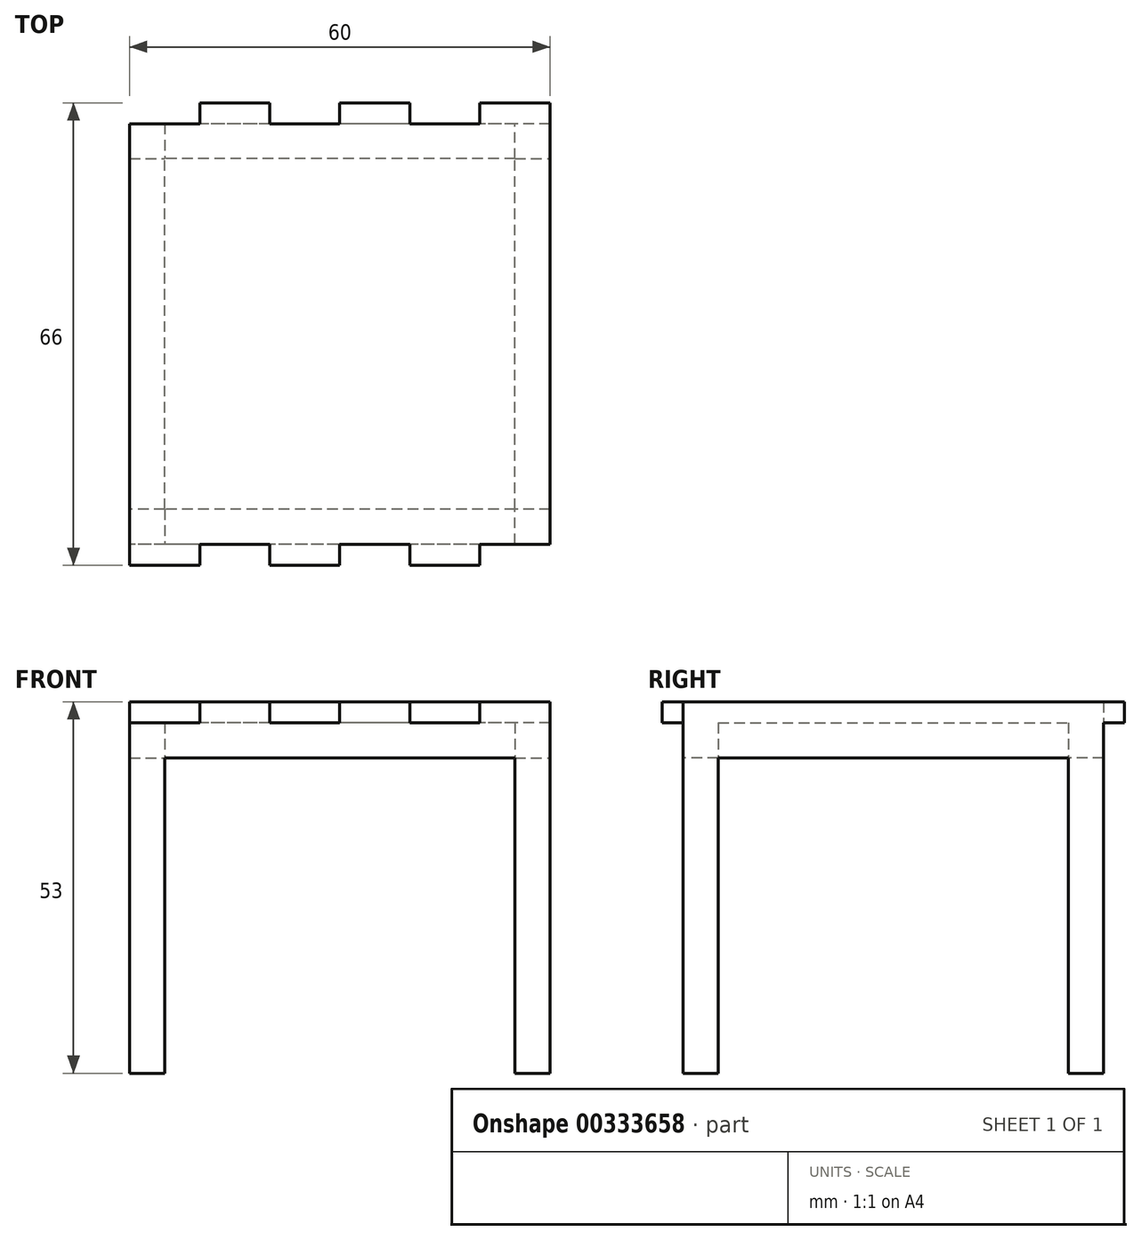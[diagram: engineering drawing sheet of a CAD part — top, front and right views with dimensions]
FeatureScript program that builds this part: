
annotation { "Feature Type Name" : "Feature", "Feature Type Description" : "" }
export const myFeature = defineFeature(function(context is Context, id is Id, definition is map)
    precondition{}
    {
        {
            var Q0;
            Q0=qCreatedBy(makeId("Top.planeOp"),FACE);
            var sketch = newSketch(context, id + "F0", { "sketchPlane" : qUnion([Q0])});
            skLineSegment(sketch, "E0.bottom", {"start": v(0, 0) * mm, "end": v(-60, 0) * mm});
            skLineSegment(sketch, "E0.top", {"start": v(0, 60) * mm, "end": v(-60, 60) * mm});
            skLineSegment(sketch, "E0.left", {"start": v(0, 0) * mm, "end": v(0, 60) * mm});
            skLineSegment(sketch, "E0.right", {"start": v(-60, 0) * mm, "end": v(-60, 60) * mm});
            skLineSegment(sketch, "E1.0", {"start": v(-5, 5) * mm, "end": v(-55, 5) * mm});
            skLineSegment(sketch, "E1.1", {"start": v(-5, 5) * mm, "end": v(-5, 55) * mm});
            skLineSegment(sketch, "E1.2", {"start": v(-5, 55) * mm, "end": v(-55, 55) * mm});
            skLineSegment(sketch, "E1.3", {"start": v(-55, 5) * mm, "end": v(-55, 55) * mm});
            skSolve(sketch);
        }
        {
            var Q0;
            Q0 = qSketchRegion(id + "F0", true);
            extrude(context, id + "F1", {"entities" : qUnion([Q0]), "depth" : 5 * mm});
        }
        {
            var Q0;
            Q0=makeQuery(id+"F1.opExtrude","CAP_FACE",FACE,{"disambiguationData":[OSD([sQuery(id+"F0.wireOp",EDGE,"E0.bottom"),sQuery(id+"F0.wireOp",EDGE,"E0.top"),sQuery(id+"F0.wireOp",EDGE,"E0.left"),sQuery(id+"F0.wireOp",EDGE,"E0.right"),sQuery(id+"F0.wireOp",EDGE,"E1.0"),sQuery(id+"F0.wireOp",EDGE,"E1.1"),sQuery(id+"F0.wireOp",EDGE,"E1.2"),sQuery(id+"F0.wireOp",EDGE,"E1.3")])],"isStart":true});
            var sketch = newSketch(context, id + "F2", { "sketchPlane" : qUnion([Q0])});
            skLineSegment(sketch, "E2.bottom", {"start": v(0, 0) * mm, "end": v(-5, 0) * mm});
            skLineSegment(sketch, "E2.top", {"start": v(0, -5) * mm, "end": v(-5, -5) * mm});
            skLineSegment(sketch, "E2.left", {"start": v(0, 0) * mm, "end": v(0, -5) * mm});
            skLineSegment(sketch, "E2.right", {"start": v(-5, 0) * mm, "end": v(-5, -5) * mm});
            skLineSegment(sketch, "E3.bottom", {"start": v(-55, -5) * mm, "end": v(-60, -5) * mm});
            skLineSegment(sketch, "E3.top", {"start": v(-55, 0) * mm, "end": v(-60, 0) * mm});
            skLineSegment(sketch, "E3.left", {"start": v(-55, -5) * mm, "end": v(-55, 0) * mm});
            skLineSegment(sketch, "E3.right", {"start": v(-60, -5) * mm, "end": v(-60, 0) * mm});
            skLineSegment(sketch, "E4.bottom", {"start": v(-5, -55) * mm, "end": v(0, -55) * mm});
            skLineSegment(sketch, "E4.top", {"start": v(-5, -60) * mm, "end": v(0, -60) * mm});
            skLineSegment(sketch, "E4.left", {"start": v(-5, -55) * mm, "end": v(-5, -60) * mm});
            skLineSegment(sketch, "E4.right", {"start": v(0, -55) * mm, "end": v(0, -60) * mm});
            skLineSegment(sketch, "E5.bottom", {"start": v(-60, -60) * mm, "end": v(-55, -60) * mm});
            skLineSegment(sketch, "E5.top", {"start": v(-60, -55) * mm, "end": v(-55, -55) * mm});
            skLineSegment(sketch, "E5.left", {"start": v(-60, -60) * mm, "end": v(-60, -55) * mm});
            skLineSegment(sketch, "E5.right", {"start": v(-55, -60) * mm, "end": v(-55, -55) * mm});
            skSolve(sketch);
        }
        {
            var Q0;
            Q0 = qSketchRegion(id + "F2", true);
            extrude(context, id + "F3", {"entities" : qUnion([Q0]), "operationType" : NewBodyOperationType.ADD, "depth" : 45 * mm});
        }
        {
            var Q0;
            Q0=makeQuery(id+"F1.opExtrude","CAP_FACE",FACE,{"disambiguationData":[OSD([sQuery(id+"F0.wireOp",EDGE,"E0.bottom"),sQuery(id+"F0.wireOp",EDGE,"E0.top"),sQuery(id+"F0.wireOp",EDGE,"E0.left"),sQuery(id+"F0.wireOp",EDGE,"E0.right"),sQuery(id+"F0.wireOp",EDGE,"E1.0"),sQuery(id+"F0.wireOp",EDGE,"E1.1"),sQuery(id+"F0.wireOp",EDGE,"E1.2"),sQuery(id+"F0.wireOp",EDGE,"E1.3")])],"isStart":false});
            var sketch = newSketch(context, id + "F4", { "sketchPlane" : qUnion([Q0])});
            skLineSegment(sketch, "E6.bottom", {"start": v(0, 0) * mm, "end": v(-10, 0) * mm});
            skLineSegment(sketch, "E6.top", {"start": v(0, 63) * mm, "end": v(-10, 63) * mm});
            skLineSegment(sketch, "E6.left", {"start": v(0, 0) * mm, "end": v(0, 63) * mm});
            skLineSegment(sketch, "E6.right", {"start": v(-10, 0) * mm, "end": v(-10, 63) * mm});
            skLineSegment(sketch, "E7.bottom", {"start": v(-10, 60) * mm, "end": v(-20, 60) * mm});
            skLineSegment(sketch, "E7.top", {"start": v(-10, -3) * mm, "end": v(-20, -3) * mm});
            skLineSegment(sketch, "E7.left", {"start": v(-10, 60) * mm, "end": v(-10, -3) * mm});
            skLineSegment(sketch, "E7.right", {"start": v(-20, 60) * mm, "end": v(-20, -3) * mm});
            skPoint(sketch, "E8.oppositeSnap0", {"position": v(-30, 5) * mm});
            skLineSegment(sketch, "E8.bottom", {"start": v(-20, 0) * mm, "end": v(-30, 0) * mm});
            skLineSegment(sketch, "E8.top", {"start": v(-20, 63) * mm, "end": v(-30, 63) * mm});
            skLineSegment(sketch, "E8.left", {"start": v(-20, 0) * mm, "end": v(-20, 63) * mm});
            skLineSegment(sketch, "E8.right", {"start": v(-30, 0) * mm, "end": v(-30, 63) * mm});
            skLineSegment(sketch, "E9.bottom", {"start": v(-30, 60) * mm, "end": v(-40, 60) * mm});
            skLineSegment(sketch, "E9.top", {"start": v(-30, -3) * mm, "end": v(-40, -3) * mm});
            skLineSegment(sketch, "E9.left", {"start": v(-30, 60) * mm, "end": v(-30, -3) * mm});
            skLineSegment(sketch, "E9.right", {"start": v(-40, 60) * mm, "end": v(-40, -3) * mm});
            skLineSegment(sketch, "E10.bottom", {"start": v(-40, 0) * mm, "end": v(-50, 0) * mm});
            skLineSegment(sketch, "E10.top", {"start": v(-40, 63) * mm, "end": v(-50, 63) * mm});
            skLineSegment(sketch, "E10.left", {"start": v(-40, 0) * mm, "end": v(-40, 63) * mm});
            skLineSegment(sketch, "E10.right", {"start": v(-50, 0) * mm, "end": v(-50, 63) * mm});
            skPoint(sketch, "E11.oppositeSnap0", {"position": v(-60, 30) * mm});
            skLineSegment(sketch, "E11.bottom", {"start": v(-50, 60) * mm, "end": v(-60, 60) * mm});
            skLineSegment(sketch, "E11.top", {"start": v(-50, -3) * mm, "end": v(-60, -3) * mm});
            skLineSegment(sketch, "E11.left", {"start": v(-50, 60) * mm, "end": v(-50, -3) * mm});
            skLineSegment(sketch, "E11.right", {"start": v(-60, 60) * mm, "end": v(-60, -3) * mm});
            skSolve(sketch);
        }
        {
            var Q0;
            Q0 = qSketchRegion(id + "F4", true);
            extrude(context, id + "F5", {"entities" : qUnion([Q0]), "operationType" : NewBodyOperationType.ADD, "depth" : 3 * mm});
        }
    });
